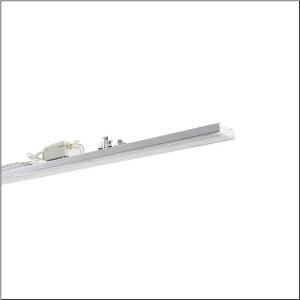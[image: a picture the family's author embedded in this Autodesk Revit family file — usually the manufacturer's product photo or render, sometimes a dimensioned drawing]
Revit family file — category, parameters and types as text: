
# Revit family: licross_r__21_recessed_ho_52tl1ecn4axs_dc99
name_source: partatom
category: Lighting Fixtures
units: mm (PartAtom-declared; Revit-internal decimal feet)

## family parameters
Cut with Voids When Loaded = No
Host = Face
Light Source = No
Part Type = Normal
Room Calculation Point = No
Round Connector Dimension = Use Diameter
Shared = No

## types (1)
- --- (1 x LED, 10030 lm, 54.7 W, 4000K)
    Apparent Load = 55 VA
    CIE Flux Codes = 85 95 99 100 100
    Color Rendering = 80
    Color Temperature = 4000K
    Default Elevation = 1800 mm
    Description = Licross® 21 Recessed HO, luminaire insert, of sheet steel, galvanised, coil coated, white, length: 1.500mm, width: 66mm, height: 67mm, LED rated luminous flux: 10.030lm, light colour: 840, control gear: ON/OFF Multilumen, CLOi, control gear: ECG Multilumen, with plug, 3-pole, with phase selection, mains connection: 220..240V, AC, 50/60Hz, start of lifetime: 55W, end of service life: 66W, halogen-free wiring, primary light control with lens, of plastic, primary optical cover: cover, of PMMA, light emission: direct distribution, primary light characteristic: symmetric, protection rating (complete): IP40, insulation class (complete): insulation class I (protective earthing), certification: CE, ENEC, VDE, UKCA, protection symbol: D if used in an environment without relevant dust loads with corresponding accessories, impact resistance: IK06, permissible ambient temperature for indoor applications: -35..+35°C, corresponds to IFS (International Featured Standards) requirements for safety and quality in the food industry, reducing of maximum allowable ambient temperature of 5°C with ceiling mounting, LABS conformity tested according to VDMA 24364:2018-05, packaging unit: 1 piece
    Height = 58 mm
    Lamp = 1 x LED
    Lamp Light Flux = 10030 lm
    Lamp Power = 54.7 W
    Lamp count = 1
    Length = 1500 mm
    Luminous efficacy = 183 lm/W
    Manufacturer = Siteco
    ModVariant = No
    Model = 52TL1ECN4AXS
    Mounting Place = Ceiling
    Mounting Type = Pendant
    Number of Poles = 1
    OnlyDefault = Yes
    Power Factor = 1
    Product Name = Licross® 21 Recessed HO
    Product group = luminaire insert
    ProductGroupID = 901
    Protection Class = Protection class I
    Protection Degree = IP 40
    RLX_Detail_Level = 1
    RLX_Emergency_Light_Flux = 0 lm
    RLX_Emergency_Type = 0
    RLX_Emergency_Type_DB = No
    RlxData = <blob elided: 22453 chars, md5=d0833a6c>
    Socket = socket
    Standby Power = 0 W
    System Light Flux = 10030 lm
    System Power = 55 W
    Type Comments = factory setting: luminous flux: 100 % | (A | C | E) | 129 mA
    Type Image = l_1296930.jpg
    URL = http://relux.com
    VarID = @adj_040049
    Voltage = 0 V
    Weight = 0.00 kg
    Width = 66 mm

## geometry (parser evidence)
native form markers: Blend x4, Sweep x10
no freeform markers — native parametric forms only
